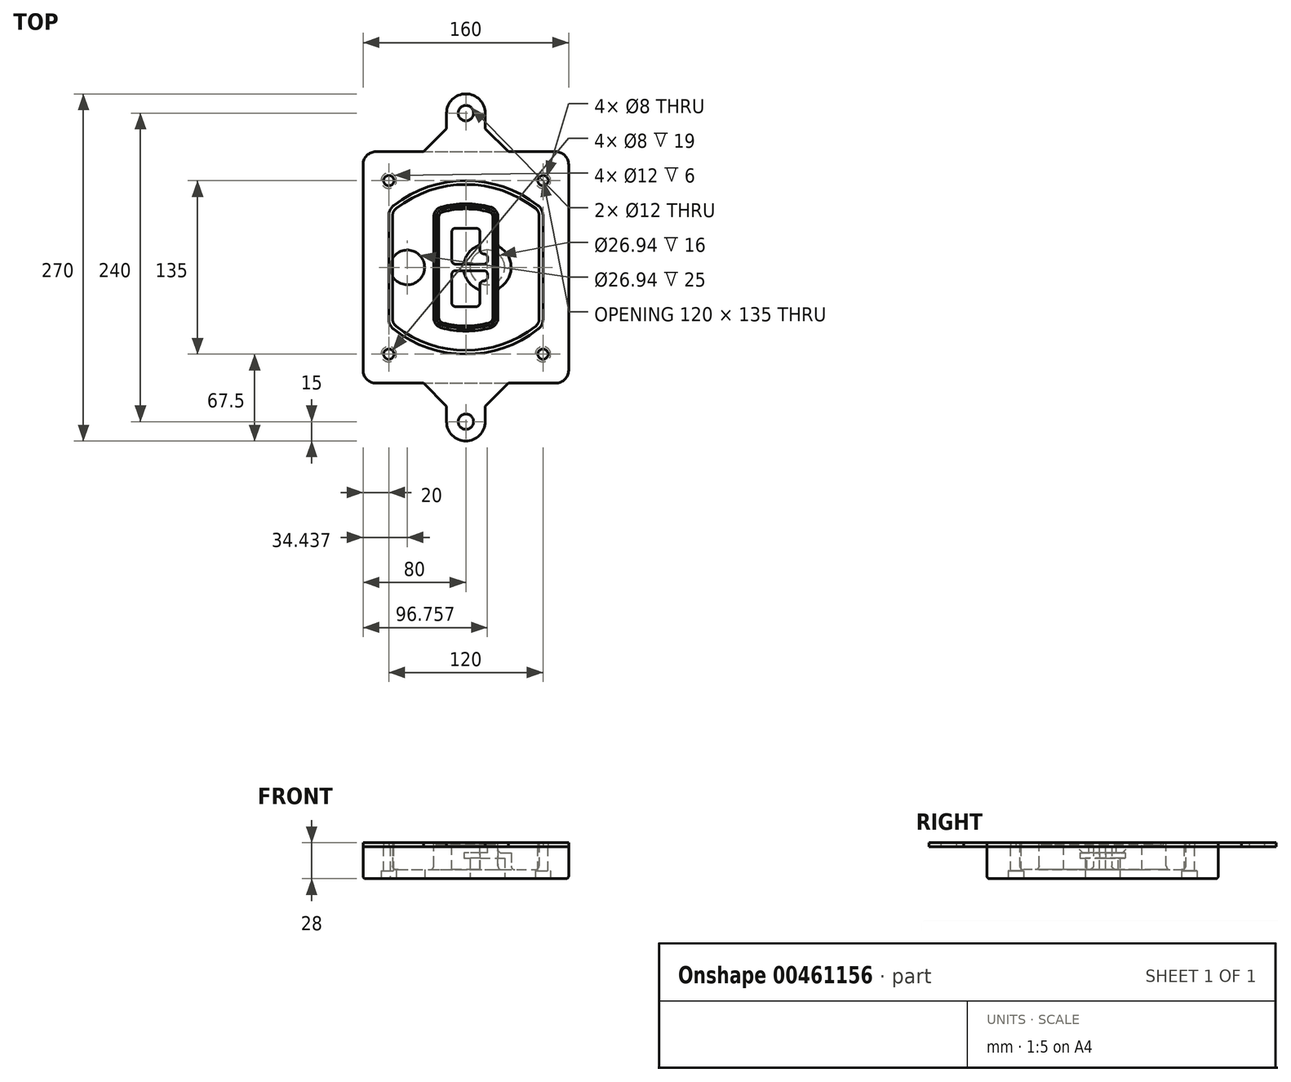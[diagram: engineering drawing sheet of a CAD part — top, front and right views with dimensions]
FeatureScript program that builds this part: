
annotation { "Feature Type Name" : "Feature", "Feature Type Description" : "" }
export const myFeature = defineFeature(function(context is Context, id is Id, definition is map)
    precondition{}
    {
        {
            var Q0;
            Q0=qCreatedBy(makeId("Top.planeOp"),FACE);
            var sketch = newSketch(context, id + "F0", { "sketchPlane" : qUnion([Q0])});
            skPoint(sketch, "E0.rect.middle", {"position": v(0, 0) * mm});
            skLineSegment(sketch, "E1.bottom", {"start": v(-70, -90) * mm, "end": v(70, -90) * mm});
            skLineSegment(sketch, "E1.top", {"start": v(-70, 90) * mm, "end": v(70, 90) * mm});
            skLineSegment(sketch, "E1.left", {"start": v(-80, -80) * mm, "end": v(-80, 80) * mm});
            skLineSegment(sketch, "E1.right", {"start": v(80, -80) * mm, "end": v(80, 80) * mm});
            skLineSegment(sketch, "E2", {"start": v(-80, 90) * mm, "end": v(80, -90) * mm, "construction": true});
            skLineSegment(sketch, "E3", {"start": v(80, 90) * mm, "end": v(-80, -90) * mm, "construction": true});
            skCircle(sketch, "E4", {"center": v(-60, 67.5) * mm, "radius": 4 * mm});
            skCircle(sketch, "E5", {"center": v(60, 67.5) * mm, "radius": 4 * mm});
            skCircle(sketch, "E6", {"center": v(60, -67.5) * mm, "radius": 4 * mm});
            skCircle(sketch, "E7", {"center": v(-60, -67.5) * mm, "radius": 4 * mm});
            skLineSegment(sketch, "E8", {"start": v(-60, 67.5) * mm, "end": v(60, 67.5) * mm, "construction": true});
            skLineSegment(sketch, "E9", {"start": v(60, 67.5) * mm, "end": v(60, -67.5) * mm, "construction": true});
            skLineSegment(sketch, "E10", {"start": v(60, -67.5) * mm, "end": v(-60, -67.5) * mm, "construction": true});
            skLineSegment(sketch, "E11", {"start": v(-60, -67.5) * mm, "end": v(-60, 67.5) * mm, "construction": true});
            skLineSegment(sketch, "E12", {"start": v(-60, 40.3) * mm, "end": v(-60, -40.3) * mm});
            skLineSegment(sketch, "E13", {"start": v(60, 40.3) * mm, "end": v(60, -40.3) * mm});
            skArc(sketch, "E14", {"start": v(56.15, 48.18) * mm, "mid": v(0, 67.5) * mm, "end": v(-56.15, 48.18) * mm});
            skArc(sketch, "E15", {"start": v(-56.15, -48.18) * mm, "mid": v(0, -67.5) * mm, "end": v(56.15, -48.18) * mm});
            skLineSegment(sketch, "E16", {"start": v(-60, 0) * mm, "end": v(60, 0) * mm, "construction": true});
            skPoint(sketch, "E17.visualSharp", {"position": v(-60, -45) * mm});
            skArc(sketch, "E17.filletArc", {"start": v(-60, -40.3) * mm, "mid": v(-58.99, -44.68) * mm, "end": v(-56.15, -48.18) * mm});
            skPoint(sketch, "E18.visualSharp", {"position": v(-60, 45) * mm});
            skArc(sketch, "E18.filletArc", {"start": v(-56.15, 48.18) * mm, "mid": v(-58.99, 44.68) * mm, "end": v(-60, 40.3) * mm});
            skPoint(sketch, "E19.visualSharp", {"position": v(60, 45) * mm});
            skArc(sketch, "E19.filletArc", {"start": v(60, 40.3) * mm, "mid": v(58.99, 44.68) * mm, "end": v(56.15, 48.18) * mm});
            skPoint(sketch, "E20.visualSharp", {"position": v(60, -45) * mm});
            skArc(sketch, "E20.filletArc", {"start": v(56.15, -48.18) * mm, "mid": v(58.99, -44.68) * mm, "end": v(60, -40.3) * mm});
            skPoint(sketch, "E21.visualSharp", {"position": v(-80, 90) * mm});
            skArc(sketch, "E21.filletArc", {"start": v(-70, 90) * mm, "mid": v(-77.07, 87.07) * mm, "end": v(-80, 80) * mm});
            skPoint(sketch, "E22.visualSharp", {"position": v(80, 90) * mm});
            skArc(sketch, "E22.filletArc", {"start": v(80, 80) * mm, "mid": v(77.07, 87.07) * mm, "end": v(70, 90) * mm});
            skPoint(sketch, "E23.visualSharp", {"position": v(80, -90) * mm});
            skArc(sketch, "E23.filletArc", {"start": v(70, -90) * mm, "mid": v(77.07, -87.07) * mm, "end": v(80, -80) * mm});
            skPoint(sketch, "E24.visualSharp", {"position": v(-80, -90) * mm});
            skArc(sketch, "E24.filletArc", {"start": v(-80, -80) * mm, "mid": v(-77.07, -87.07) * mm, "end": v(-70, -90) * mm});
            skArc(sketch, "E25.0", {"start": v(57, 40.3) * mm, "mid": v(56.3, 43.36) * mm, "end": v(54.3, 45.81) * mm});
            skLineSegment(sketch, "E25.1", {"start": v(57, 40.3) * mm, "end": v(57, -40.3) * mm});
            skArc(sketch, "E25.2", {"start": v(54.3, -45.81) * mm, "mid": v(56.3, -43.36) * mm, "end": v(57, -40.3) * mm});
            skArc(sketch, "E25.3", {"start": v(-54.3, -45.81) * mm, "mid": v(0, -64.5) * mm, "end": v(54.3, -45.81) * mm});
            skArc(sketch, "E25.4", {"start": v(-57, -40.3) * mm, "mid": v(-56.3, -43.36) * mm, "end": v(-54.3, -45.81) * mm});
            skArc(sketch, "E25.5", {"start": v(54.3, 45.81) * mm, "mid": v(0, 64.5) * mm, "end": v(-54.3, 45.81) * mm});
            skLineSegment(sketch, "E25.6", {"start": v(-57, 40.3) * mm, "end": v(-57, -40.3) * mm});
            skArc(sketch, "E25.7", {"start": v(-54.3, 45.81) * mm, "mid": v(-56.3, 43.36) * mm, "end": v(-57, 40.3) * mm});
            skArc(sketch, "E26.0", {"start": v(-58.62, 51.33) * mm, "mid": v(-62.58, 46.43) * mm, "end": v(-64, 40.3) * mm});
            skArc(sketch, "E26.1", {"start": v(58.62, 51.33) * mm, "mid": v(0, 71.5) * mm, "end": v(-58.62, 51.33) * mm});
            skArc(sketch, "E26.2", {"start": v(64, 40.3) * mm, "mid": v(62.58, 46.43) * mm, "end": v(58.62, 51.33) * mm});
            skLineSegment(sketch, "E26.3", {"start": v(64, 40.3) * mm, "end": v(64, -40.3) * mm});
            skArc(sketch, "E26.4", {"start": v(58.62, -51.33) * mm, "mid": v(62.58, -46.43) * mm, "end": v(64, -40.3) * mm});
            skLineSegment(sketch, "E26.5", {"start": v(-64, 40.3) * mm, "end": v(-64, -40.3) * mm});
            skArc(sketch, "E26.6", {"start": v(-58.62, -51.33) * mm, "mid": v(0, -71.5) * mm, "end": v(58.62, -51.33) * mm});
            skArc(sketch, "E26.7", {"start": v(-64, -40.3) * mm, "mid": v(-62.58, -46.43) * mm, "end": v(-58.62, -51.33) * mm});
            skSolve(sketch);
        }
        {
            var Q0;
            Q0=makeQuery(id+"F0.imprint","IMPRINT",FACE,{"disambiguationData":[TD([[makeQuery(id+"F0.imprint","IMPRINT",EDGE,{"derivedFrom":sQuery(id+"F0.wireOp",EDGE,"E1.bottom")}),1.0]])]});
            var Q1;
            Q1=makeQuery(id+"F0.imprint","IMPRINT",FACE,{"disambiguationData":[TD([[makeQuery(id+"F0.imprint","IMPRINT",EDGE,{"derivedFrom":sQuery(id+"F0.wireOp",EDGE,"E12")}),1.0]])]});
            var Q2;
            Q2=makeQuery(id+"F0.imprint","IMPRINT",FACE,{"disambiguationData":[TD([[makeQuery(id+"F0.imprint","IMPRINT",EDGE,{"derivedFrom":sQuery(id+"F0.wireOp",EDGE,"E25.0")}),1.0]])]});
            var Q3;
            Q3=makeQuery(id+"F0.imprint","IMPRINT",FACE,{"disambiguationData":[TD([[makeQuery(id+"F0.imprint","IMPRINT",EDGE,{"derivedFrom":sQuery(id+"F0.wireOp",EDGE,"E12")}),-1.0]])]});
            extrude(context, id + "F1", {"entities" : qUnion([Q0, Q1, Q2, Q3]), "oppositeDirection" : true, "depth" : 25 * mm});
        }
        {
            var Q0;
            Q0=makeQuery(id+"F0.imprint","IMPRINT",FACE,{"disambiguationData":[TD([[makeQuery(id+"F0.imprint","IMPRINT",EDGE,{"derivedFrom":sQuery(id+"F0.wireOp",EDGE,"E12")}),1.0]])]});
            extrude(context, id + "F2", {"entities" : qUnion([Q0]), "operationType" : NewBodyOperationType.ADD, "depth" : 3 * mm});
        }
        {
            var Q0;
            Q0=makeQuery(id+"F0.imprint","IMPRINT",FACE,{"disambiguationData":[TD([[makeQuery(id+"F0.imprint","IMPRINT",EDGE,{"derivedFrom":sQuery(id+"F0.wireOp",EDGE,"E25.0")}),1.0]])]});
            extrude(context, id + "F3", {"entities" : qUnion([Q0]), "operationType" : NewBodyOperationType.REMOVE, "oppositeDirection" : true, "depth" : 18 * mm});
        }
        {
            var Q0;
            Q0=makeQuery(id+"F2.opExtrude","CAP_FACE",FACE,{"disambiguationData":[OSD([sQuery(id+"F0.wireOp",EDGE,"E12"),sQuery(id+"F0.wireOp",EDGE,"E13"),sQuery(id+"F0.wireOp",EDGE,"E14"),sQuery(id+"F0.wireOp",EDGE,"E15"),sQuery(id+"F0.wireOp",EDGE,"E17.filletArc"),sQuery(id+"F0.wireOp",EDGE,"E18.filletArc"),sQuery(id+"F0.wireOp",EDGE,"E19.filletArc"),sQuery(id+"F0.wireOp",EDGE,"E20.filletArc"),sQuery(id+"F0.wireOp",EDGE,"E25.0"),sQuery(id+"F0.wireOp",EDGE,"E25.1"),sQuery(id+"F0.wireOp",EDGE,"E25.2"),sQuery(id+"F0.wireOp",EDGE,"E25.3"),sQuery(id+"F0.wireOp",EDGE,"E25.4"),sQuery(id+"F0.wireOp",EDGE,"E25.5"),sQuery(id+"F0.wireOp",EDGE,"E25.6"),sQuery(id+"F0.wireOp",EDGE,"E25.7")])],"isStart":false});
            var sketch = newSketch(context, id + "F4", { "sketchPlane" : qUnion([Q0])});
            skArc(sketch, "E27.0", {"start": v(-19.08, -46.97) * mm, "mid": v(0, -49.5) * mm, "end": v(19.08, -46.97) * mm});
            skArc(sketch, "E28.0", {"start": v(19.08, 46.97) * mm, "mid": v(0, 49.5) * mm, "end": v(-19.08, 46.97) * mm});
            skLineSegment(sketch, "E29", {"start": v(-25, 39.25) * mm, "end": v(-25, -39.25) * mm});
            skLineSegment(sketch, "E30", {"start": v(25, 39.25) * mm, "end": v(25, -39.25) * mm});
            skLineSegment(sketch, "E31", {"start": v(-25, 45.1) * mm, "end": v(25, 45.1) * mm, "construction": true});
            skLineSegment(sketch, "E32", {"start": v(-25, -45.1) * mm, "end": v(25, -45.1) * mm, "construction": true});
            skPoint(sketch, "E33.visualSharp", {"position": v(-25, 45.1) * mm});
            skArc(sketch, "E33.filletArc", {"start": v(-19.08, 46.97) * mm, "mid": v(-23.35, 44.11) * mm, "end": v(-25, 39.25) * mm});
            skPoint(sketch, "E34.visualSharp", {"position": v(25, 45.1) * mm});
            skArc(sketch, "E34.filletArc", {"start": v(25, 39.25) * mm, "mid": v(23.35, 44.11) * mm, "end": v(19.08, 46.97) * mm});
            skPoint(sketch, "E35.visualSharp", {"position": v(25, -45.1) * mm});
            skArc(sketch, "E35.filletArc", {"start": v(19.08, -46.97) * mm, "mid": v(23.35, -44.11) * mm, "end": v(25, -39.25) * mm});
            skPoint(sketch, "E36.visualSharp", {"position": v(-25, -45.1) * mm});
            skArc(sketch, "E36.filletArc", {"start": v(-25, -39.25) * mm, "mid": v(-23.35, -44.11) * mm, "end": v(-19.08, -46.97) * mm});
            skArc(sketch, "E37.0", {"start": v(54.3, 45.81) * mm, "mid": v(0, 64.5) * mm, "end": v(-54.3, 45.81) * mm});
            skArc(sketch, "E37.1", {"start": v(-54.3, 45.81) * mm, "mid": v(-56.3, 43.36) * mm, "end": v(-57, 40.3) * mm});
            skLineSegment(sketch, "E37.2", {"start": v(-57, 40.3) * mm, "end": v(-57, -40.3) * mm});
            skArc(sketch, "E37.3", {"start": v(-57, -40.3) * mm, "mid": v(-56.3, -43.36) * mm, "end": v(-54.3, -45.81) * mm});
            skArc(sketch, "E37.4", {"start": v(-54.3, -45.81) * mm, "mid": v(0, -64.5) * mm, "end": v(54.3, -45.81) * mm});
            skArc(sketch, "E37.5", {"start": v(54.3, -45.81) * mm, "mid": v(56.3, -43.36) * mm, "end": v(57, -40.3) * mm});
            skLineSegment(sketch, "E37.6", {"start": v(57, 40.3) * mm, "end": v(57, -40.3) * mm});
            skArc(sketch, "E37.7", {"start": v(57, 40.3) * mm, "mid": v(56.3, 43.36) * mm, "end": v(54.3, 45.81) * mm});
            skLineSegment(sketch, "E38.0", {"start": v(23, 39.25) * mm, "end": v(23, -39.25) * mm});
            skArc(sketch, "E38.1", {"start": v(18.56, -45.04) * mm, "mid": v(21.76, -42.9) * mm, "end": v(23, -39.25) * mm});
            skArc(sketch, "E38.2", {"start": v(-18.56, -45.04) * mm, "mid": v(0, -47.5) * mm, "end": v(18.56, -45.04) * mm});
            skArc(sketch, "E38.3", {"start": v(-23, -39.25) * mm, "mid": v(-21.76, -42.9) * mm, "end": v(-18.56, -45.04) * mm});
            skLineSegment(sketch, "E38.4", {"start": v(-23, 39.25) * mm, "end": v(-23, -39.25) * mm});
            skArc(sketch, "E38.5", {"start": v(23, 39.25) * mm, "mid": v(21.76, 42.9) * mm, "end": v(18.56, 45.04) * mm});
            skArc(sketch, "E38.6", {"start": v(-18.56, 45.04) * mm, "mid": v(-21.76, 42.9) * mm, "end": v(-23, 39.25) * mm});
            skArc(sketch, "E38.7", {"start": v(18.56, 45.04) * mm, "mid": v(0, 47.5) * mm, "end": v(-18.56, 45.04) * mm});
            skArc(sketch, "E39.0", {"start": v(21, 39.25) * mm, "mid": v(20.18, 41.68) * mm, "end": v(18.04, 43.1) * mm});
            skLineSegment(sketch, "E39.1", {"start": v(21, 39.25) * mm, "end": v(21, -39.25) * mm});
            skArc(sketch, "E39.2", {"start": v(18.04, -43.1) * mm, "mid": v(20.18, -41.68) * mm, "end": v(21, -39.25) * mm});
            skArc(sketch, "E39.3", {"start": v(-18.04, -43.1) * mm, "mid": v(0, -45.5) * mm, "end": v(18.04, -43.1) * mm});
            skArc(sketch, "E39.4", {"start": v(-21, -39.25) * mm, "mid": v(-20.18, -41.68) * mm, "end": v(-18.04, -43.1) * mm});
            skArc(sketch, "E39.5", {"start": v(18.04, 43.1) * mm, "mid": v(0, 45.5) * mm, "end": v(-18.04, 43.1) * mm});
            skLineSegment(sketch, "E39.6", {"start": v(-21, 39.25) * mm, "end": v(-21, -39.25) * mm});
            skArc(sketch, "E39.7", {"start": v(-18.04, 43.1) * mm, "mid": v(-20.18, 41.68) * mm, "end": v(-21, 39.25) * mm});
            skLineSegment(sketch, "E40", {"start": v(-25, 0) * mm, "end": v(25, 0) * mm, "construction": true});
            skLineSegment(sketch, "E41", {"start": v(-11, 5.5) * mm, "end": v(-11, 27.5) * mm});
            skLineSegment(sketch, "E42", {"start": v(-8, 30.5) * mm, "end": v(8, 30.5) * mm});
            skLineSegment(sketch, "E43", {"start": v(11, 27.5) * mm, "end": v(11, 13.5) * mm});
            skLineSegment(sketch, "E44", {"start": v(14, 10.5) * mm, "end": v(14, 10.5) * mm});
            skLineSegment(sketch, "E45", {"start": v(17, 7.5) * mm, "end": v(17, 5.5) * mm});
            skLineSegment(sketch, "E46", {"start": v(14, 2.5) * mm, "end": v(-8, 2.5) * mm});
            skPoint(sketch, "E47.visualSharp", {"position": v(-11, 30.5) * mm});
            skArc(sketch, "E47.filletArc", {"start": v(-8, 30.5) * mm, "mid": v(-10.12, 29.62) * mm, "end": v(-11, 27.5) * mm});
            skPoint(sketch, "E48.visualSharp", {"position": v(11, 30.5) * mm});
            skArc(sketch, "E48.filletArc", {"start": v(11, 27.5) * mm, "mid": v(10.12, 29.62) * mm, "end": v(8, 30.5) * mm});
            skPoint(sketch, "E49.visualSharp", {"position": v(11, 10.5) * mm});
            skArc(sketch, "E49.filletArc", {"start": v(11, 13.5) * mm, "mid": v(11.88, 11.38) * mm, "end": v(14, 10.5) * mm});
            skPoint(sketch, "E50.visualSharp", {"position": v(17, 10.5) * mm});
            skArc(sketch, "E50.filletArc", {"start": v(17, 7.5) * mm, "mid": v(16.12, 9.62) * mm, "end": v(14, 10.5) * mm});
            skPoint(sketch, "E51.visualSharp", {"position": v(17, 2.5) * mm});
            skArc(sketch, "E51.filletArc", {"start": v(14, 2.5) * mm, "mid": v(16.12, 3.38) * mm, "end": v(17, 5.5) * mm});
            skPoint(sketch, "E52.visualSharp", {"position": v(-11, 2.5) * mm});
            skArc(sketch, "E52.filletArc", {"start": v(-11, 5.5) * mm, "mid": v(-10.12, 3.38) * mm, "end": v(-8, 2.5) * mm});
            skLineSegment(sketch, "E53.0.MirrorCS", {"start": v(14, -2.5) * mm, "end": v(-8, -2.5) * mm});
            skArc(sketch, "E54.0.MirrorCS", {"start": v(-11, -5.5) * mm, "mid": v(-10.12, -3.38) * mm, "end": v(-8, -2.5) * mm});
            skLineSegment(sketch, "E55.0.MirrorCS", {"start": v(-11, -5.5) * mm, "end": v(-11, -27.5) * mm});
            skArc(sketch, "E56.0.MirrorCS", {"start": v(-8, -30.5) * mm, "mid": v(-10.12, -29.62) * mm, "end": v(-11, -27.5) * mm});
            skLineSegment(sketch, "E57.0.MirrorCS", {"start": v(-8, -30.5) * mm, "end": v(8, -30.5) * mm});
            skArc(sketch, "E58.0.MirrorCS", {"start": v(11, -27.5) * mm, "mid": v(10.12, -29.62) * mm, "end": v(8, -30.5) * mm});
            skLineSegment(sketch, "E59.0.MirrorCS", {"start": v(11, -27.5) * mm, "end": v(11, -13.5) * mm});
            skArc(sketch, "E60.0.MirrorCS", {"start": v(11, -13.5) * mm, "mid": v(11.88, -11.38) * mm, "end": v(14, -10.5) * mm});
            skArc(sketch, "E61.0.MirrorCS", {"start": v(17, -7.5) * mm, "mid": v(16.12, -9.62) * mm, "end": v(14, -10.5) * mm});
            skLineSegment(sketch, "E62.0.MirrorCS", {"start": v(17, -7.5) * mm, "end": v(17, -5.5) * mm});
            skArc(sketch, "E63.0.MirrorCS", {"start": v(14, -2.5) * mm, "mid": v(16.12, -3.38) * mm, "end": v(17, -5.5) * mm});
            skSolve(sketch);
        }
        {
            var Q0;
            Q0=makeQuery(id+"F4.imprint","IMPRINT",FACE,{"disambiguationData":[TD([[makeQuery(id+"F4.imprint","IMPRINT",EDGE,{"derivedFrom":sQuery(id+"F4.wireOp",EDGE,"E27.0")}),1.0]])]});
            var Q1;
            Q1=makeQuery(id+"F4.imprint","IMPRINT",FACE,{"disambiguationData":[TD([[makeQuery(id+"F4.imprint","IMPRINT",EDGE,{"derivedFrom":sQuery(id+"F4.wireOp",EDGE,"E38.0")}),-1.0]])]});
            var Q2;
            Q2=makeQuery(id+"F4.imprint","IMPRINT",FACE,{"disambiguationData":[TD([[makeQuery(id+"F4.imprint","IMPRINT",EDGE,{"derivedFrom":sQuery(id+"F4.wireOp",EDGE,"E39.0")}),1.0]])]});
            extrude(context, id + "F5", {"entities" : qUnion([Q0, Q1, Q2]), "operationType" : NewBodyOperationType.ADD, "endBound" : BoundingType.UP_TO_NEXT, "oppositeDirection" : true, "depth" : 25 * mm});
        }
        {
            var Q0;
            Q0=makeQuery(id+"F4.imprint","IMPRINT",FACE,{"disambiguationData":[TD([[makeQuery(id+"F4.imprint","IMPRINT",EDGE,{"derivedFrom":sQuery(id+"F4.wireOp",EDGE,"E38.0")}),-1.0]])]});
            extrude(context, id + "F6", {"entities" : qUnion([Q0]), "operationType" : NewBodyOperationType.REMOVE, "oppositeDirection" : true, "depth" : 2 * mm});
        }
        {
            var Q0;
            Q0=makeQuery(id+"F1.opExtrude","CAP_FACE",FACE,{"disambiguationData":[OSD([sQuery(id+"F0.wireOp",EDGE,"E1.bottom"),sQuery(id+"F0.wireOp",EDGE,"E1.top"),sQuery(id+"F0.wireOp",EDGE,"E1.left"),sQuery(id+"F0.wireOp",EDGE,"E1.right"),sQuery(id+"F0.wireOp",EDGE,"E4"),sQuery(id+"F0.wireOp",EDGE,"E5"),sQuery(id+"F0.wireOp",EDGE,"E6"),sQuery(id+"F0.wireOp",EDGE,"E7"),sQuery(id+"F0.wireOp",EDGE,"E21.filletArc"),sQuery(id+"F0.wireOp",EDGE,"E22.filletArc"),sQuery(id+"F0.wireOp",EDGE,"E23.filletArc"),sQuery(id+"F0.wireOp",EDGE,"E24.filletArc")])],"isStart":false});
            var sketch = newSketch(context, id + "F7", { "sketchPlane" : qUnion([Q0])});
            skCircle(sketch, "E64", {"center": v(16.76, 0) * mm, "radius": 13.47 * mm});
            skCircle(sketch, "E65", {"center": v(-45.56, 0) * mm, "radius": 13.47 * mm});
            skLineSegment(sketch, "E66", {"start": v(80, 0) * mm, "end": v(-80, 0) * mm});
            skCircle(sketch, "E67", {"center": v(16.76, 0) * mm, "radius": 18.47 * mm});
            skCircle(sketch, "E68", {"center": v(60, -67.5) * mm, "radius": 6 * mm});
            skCircle(sketch, "E69", {"center": v(-60, -67.5) * mm, "radius": 6 * mm});
            skCircle(sketch, "E70", {"center": v(-60, 67.5) * mm, "radius": 6 * mm});
            skCircle(sketch, "E71", {"center": v(60, 67.5) * mm, "radius": 6 * mm});
            skSolve(sketch);
        }
        {
            var Q0;
            {var subQ1=sQuery(id+"F7.wireOp",EDGE,"E66");var subQ4=sQuery(id+"F7.wireOp",EDGE,"E64");var subQ6=makeQuery(id+"F7.imprint","INTERSECT",VERTEX,{"disambiguationData":[OD(0.0)],"derivedFrom":[subQ4,subQ1]});Q0=makeQuery(id+"F7.imprint","IMPRINT",FACE,{"disambiguationData":[TD([[makeQuery(id+"F7.imprint","IMPRINT",EDGE,{"disambiguationData":[TD([[subQ6,-1.0]])],"derivedFrom":subQ4}),-1.0]])]});}
            var Q1;
            {var subQ0=sQuery(id+"F7.wireOp",EDGE,"E66");var subQ1=sQuery(id+"F7.wireOp",EDGE,"E64");var subQ3=makeQuery(id+"F7.imprint","INTERSECT",VERTEX,{"disambiguationData":[OD(0.0)],"derivedFrom":[subQ1,subQ0]});Q1=makeQuery(id+"F7.imprint","IMPRINT",FACE,{"disambiguationData":[TD([[makeQuery(id+"F7.imprint","IMPRINT",EDGE,{"disambiguationData":[TD([[subQ3,-1.0]])],"derivedFrom":subQ1}),1.0]])]});}
            var Q2;
            {var subQ0=sQuery(id+"F7.wireOp",EDGE,"E66");var subQ1=sQuery(id+"F7.wireOp",EDGE,"E64");var subQ3=makeQuery(id+"F7.imprint","INTERSECT",VERTEX,{"disambiguationData":[OD(0.0)],"derivedFrom":[subQ1,subQ0]});Q2=makeQuery(id+"F7.imprint","IMPRINT",FACE,{"disambiguationData":[TD([[makeQuery(id+"F7.imprint","IMPRINT",EDGE,{"disambiguationData":[TD([[subQ3,1.0]])],"derivedFrom":subQ1}),1.0]])]});}
            var Q3;
            {var subQ1=sQuery(id+"F7.wireOp",EDGE,"E66");var subQ4=sQuery(id+"F7.wireOp",EDGE,"E64");var subQ6=makeQuery(id+"F7.imprint","INTERSECT",VERTEX,{"disambiguationData":[OD(0.0)],"derivedFrom":[subQ4,subQ1]});Q3=makeQuery(id+"F7.imprint","IMPRINT",FACE,{"disambiguationData":[TD([[makeQuery(id+"F7.imprint","IMPRINT",EDGE,{"disambiguationData":[TD([[subQ6,1.0]])],"derivedFrom":subQ4}),-1.0]])]});}
            extrude(context, id + "F8", {"entities" : qUnion([Q0, Q1, Q2, Q3]), "operationType" : NewBodyOperationType.ADD, "oppositeDirection" : true, "depth" : 20 * mm});
        }
        {
            var Q0;
            {var subQ0=sQuery(id+"F7.wireOp",EDGE,"E66");var subQ1=sQuery(id+"F7.wireOp",EDGE,"E64");var subQ3=makeQuery(id+"F7.imprint","INTERSECT",VERTEX,{"disambiguationData":[OD(0.0)],"derivedFrom":[subQ1,subQ0]});Q0=makeQuery(id+"F7.imprint","IMPRINT",FACE,{"disambiguationData":[TD([[makeQuery(id+"F7.imprint","IMPRINT",EDGE,{"disambiguationData":[TD([[subQ3,-1.0]])],"derivedFrom":subQ1}),1.0]])]});}
            var Q1;
            {var subQ0=sQuery(id+"F7.wireOp",EDGE,"E66");var subQ1=sQuery(id+"F7.wireOp",EDGE,"E64");var subQ3=makeQuery(id+"F7.imprint","INTERSECT",VERTEX,{"disambiguationData":[OD(0.0)],"derivedFrom":[subQ1,subQ0]});Q1=makeQuery(id+"F7.imprint","IMPRINT",FACE,{"disambiguationData":[TD([[makeQuery(id+"F7.imprint","IMPRINT",EDGE,{"disambiguationData":[TD([[subQ3,1.0]])],"derivedFrom":subQ1}),1.0]])]});}
            extrude(context, id + "F9", {"entities" : qUnion([Q0, Q1]), "operationType" : NewBodyOperationType.REMOVE, "oppositeDirection" : true, "depth" : 16 * mm});
        }
        {
            var Q0;
            {var subQ0=sQuery(id+"F7.wireOp",EDGE,"E66");var subQ1=sQuery(id+"F7.wireOp",EDGE,"E65");var subQ3=makeQuery(id+"F7.imprint","INTERSECT",VERTEX,{"disambiguationData":[OD(0.0)],"derivedFrom":[subQ1,subQ0]});Q0=makeQuery(id+"F7.imprint","IMPRINT",FACE,{"disambiguationData":[TD([[makeQuery(id+"F7.imprint","IMPRINT",EDGE,{"disambiguationData":[TD([[subQ3,-1.0]])],"derivedFrom":subQ1}),1.0]])]});}
            var Q1;
            {var subQ0=sQuery(id+"F7.wireOp",EDGE,"E66");var subQ1=sQuery(id+"F7.wireOp",EDGE,"E65");var subQ3=makeQuery(id+"F7.imprint","INTERSECT",VERTEX,{"disambiguationData":[OD(0.0)],"derivedFrom":[subQ1,subQ0]});Q1=makeQuery(id+"F7.imprint","IMPRINT",FACE,{"disambiguationData":[TD([[makeQuery(id+"F7.imprint","IMPRINT",EDGE,{"disambiguationData":[TD([[subQ3,1.0]])],"derivedFrom":subQ1}),1.0]])]});}
            extrude(context, id + "F10", {"entities" : qUnion([Q0, Q1]), "operationType" : NewBodyOperationType.REMOVE, "oppositeDirection" : true, "depth" : 25 * mm});
        }
        {
            var Q0;
            Q0=makeQuery(id+"F7.imprint","IMPRINT",FACE,{"disambiguationData":[TD([[makeQuery(id+"F7.imprint","IMPRINT",EDGE,{"derivedFrom":sQuery(id+"F7.wireOp",EDGE,"E68")}),1.0]])]});
            var Q1;
            Q1=makeQuery(id+"F7.imprint","IMPRINT",FACE,{"disambiguationData":[TD([[makeQuery(id+"F7.imprint","IMPRINT",EDGE,{"derivedFrom":makeQuery(id+"F1.opExtrude","CAP_EDGE",EDGE,{"disambiguationData":[OSD([sQuery(id+"F0.wireOp",EDGE,"E5")])],"isStart":false})}),-1.0]])]});
            var Q2;
            Q2=makeQuery(id+"F7.imprint","IMPRINT",FACE,{"disambiguationData":[TD([[makeQuery(id+"F7.imprint","IMPRINT",EDGE,{"derivedFrom":sQuery(id+"F7.wireOp",EDGE,"E69")}),1.0]])]});
            var Q3;
            Q3=makeQuery(id+"F7.imprint","IMPRINT",FACE,{"disambiguationData":[TD([[makeQuery(id+"F7.imprint","IMPRINT",EDGE,{"derivedFrom":makeQuery(id+"F1.opExtrude","CAP_EDGE",EDGE,{"disambiguationData":[OSD([sQuery(id+"F0.wireOp",EDGE,"E4")])],"isStart":false})}),-1.0]])]});
            var Q4;
            Q4=makeQuery(id+"F7.imprint","IMPRINT",FACE,{"disambiguationData":[TD([[makeQuery(id+"F7.imprint","IMPRINT",EDGE,{"derivedFrom":sQuery(id+"F7.wireOp",EDGE,"E70")}),1.0]])]});
            var Q5;
            Q5=makeQuery(id+"F7.imprint","IMPRINT",FACE,{"disambiguationData":[TD([[makeQuery(id+"F7.imprint","IMPRINT",EDGE,{"derivedFrom":makeQuery(id+"F1.opExtrude","CAP_EDGE",EDGE,{"disambiguationData":[OSD([sQuery(id+"F0.wireOp",EDGE,"E7")])],"isStart":false})}),-1.0]])]});
            var Q6;
            Q6=makeQuery(id+"F7.imprint","IMPRINT",FACE,{"disambiguationData":[TD([[makeQuery(id+"F7.imprint","IMPRINT",EDGE,{"derivedFrom":sQuery(id+"F7.wireOp",EDGE,"E71")}),1.0]])]});
            var Q7;
            Q7=makeQuery(id+"F7.imprint","IMPRINT",FACE,{"disambiguationData":[TD([[makeQuery(id+"F7.imprint","IMPRINT",EDGE,{"derivedFrom":makeQuery(id+"F1.opExtrude","CAP_EDGE",EDGE,{"disambiguationData":[OSD([sQuery(id+"F0.wireOp",EDGE,"E6")])],"isStart":false})}),-1.0]])]});
            extrude(context, id + "F11", {"entities" : qUnion([Q0, Q1, Q2, Q3, Q4, Q5, Q6, Q7]), "operationType" : NewBodyOperationType.REMOVE, "oppositeDirection" : true, "depth" : 6 * mm});
        }
        {
            var Q0;
            Q0=makeQuery(id+"F9.boolean.opBoolean","COPY",FACE,{"derivedFrom":makeQuery(id+"F9.opExtrude","CAP_FACE",FACE,{"disambiguationData":[OSD([sQuery(id+"F7.wireOp",EDGE,"E64")])],"isStart":false})});
            var sketch = newSketch(context, id + "F12", { "sketchPlane" : qUnion([Q0])});
            skArc(sketch, "E72.0", {"start": v(11, 17.55) * mm, "mid": v(2.57, 11.82) * mm, "end": v(-1.54, 2.5) * mm});
            skArc(sketch, "E72.1", {"start": v(-1.54, -2.5) * mm, "mid": v(2.57, -11.82) * mm, "end": v(11, -17.55) * mm});
            skLineSegment(sketch, "E73", {"start": v(-1.54, -2.5) * mm, "end": v(14, -2.5) * mm});
            skLineSegment(sketch, "E74.0", {"start": v(14, 2.5) * mm, "end": v(-1.54, 2.5) * mm});
            skArc(sketch, "E74.1", {"start": v(14, 2.5) * mm, "mid": v(16.12, 3.38) * mm, "end": v(17, 5.5) * mm});
            skLineSegment(sketch, "E74.2", {"start": v(17, 7.5) * mm, "end": v(17, 5.5) * mm});
            skArc(sketch, "E74.3", {"start": v(17, 7.5) * mm, "mid": v(16.12, 9.62) * mm, "end": v(14, 10.5) * mm});
            skArc(sketch, "E74.4", {"start": v(11, 13.5) * mm, "mid": v(11.88, 11.38) * mm, "end": v(14, 10.5) * mm});
            skLineSegment(sketch, "E74.5", {"start": v(11, 17.55) * mm, "end": v(11, 13.5) * mm});
            skLineSegment(sketch, "E74.7", {"start": v(14, -2.5) * mm, "end": v(-1.54, -2.5) * mm});
            skArc(sketch, "E74.8", {"start": v(14, -2.5) * mm, "mid": v(16.12, -3.38) * mm, "end": v(17, -5.5) * mm});
            skLineSegment(sketch, "E74.9", {"start": v(17, -7.5) * mm, "end": v(17, -5.5) * mm});
            skArc(sketch, "E74.10", {"start": v(17, -7.5) * mm, "mid": v(16.12, -9.62) * mm, "end": v(14, -10.5) * mm});
            skArc(sketch, "E74.11", {"start": v(11, -13.5) * mm, "mid": v(11.88, -11.38) * mm, "end": v(14, -10.5) * mm});
            skLineSegment(sketch, "E74.12", {"start": v(11, -17.55) * mm, "end": v(11, -13.5) * mm});
            skPoint(sketch, "E75.orphan", {"position": v(11, -27.5) * mm});
            skPoint(sketch, "E76.orphan", {"position": v(-8, -2.5) * mm});
            skPoint(sketch, "E77.orphan", {"position": v(-8, 2.5) * mm});
            skPoint(sketch, "E78.orphan", {"position": v(11, 27.5) * mm});
            skSolve(sketch);
        }
        {
            var Q0;
            {var subQ7=sQuery(id+"F12.wireOp",EDGE,"E72.0");var subQ14=sQuery(id+"F12.wireOp",EDGE,"E72.1");var subQ16=sQuery(id+"F12.wireOp",EDGE,"E74.1");var subQ18=sQuery(id+"F12.wireOp",EDGE,"E74.8");Q0=qUnion([makeQuery(id+"F12.imprint","IMPRINT",FACE,{"disambiguationData":[TD([[makeQuery(id+"F12.imprint","IMPRINT",EDGE,{"derivedFrom":subQ7}),1.0]])]}),makeQuery(id+"F12.imprint","IMPRINT",FACE,{"disambiguationData":[TD([[makeQuery(id+"F12.imprint","IMPRINT",EDGE,{"derivedFrom":subQ14}),1.0]])]}),makeQuery(id+"F12.imprint","IMPRINT",FACE,{"disambiguationData":[TD([[makeQuery(id+"F12.imprint","IMPRINT",EDGE,{"derivedFrom":subQ16}),1.0]])]}),makeQuery(id+"F12.imprint","IMPRINT",FACE,{"disambiguationData":[TD([[makeQuery(id+"F12.imprint","IMPRINT",EDGE,{"derivedFrom":subQ18}),-1.0]])]})]);}
            var Q1;
            Q1=makeQuery(id+"F5.boolean.opBoolean","SPLIT",FACE,{"disambiguationData":[TD([makeQuery(id+"F5.opExtrude","SWEPT_FACE",FACE,{"disambiguationData":[OSD([sQuery(id+"F4.wireOp",EDGE,"E41")])]})])],"derivedFrom":makeQuery(id+"F3.boolean.opBoolean","COPY",FACE,{"derivedFrom":makeQuery(id+"F3.opExtrude","CAP_FACE",FACE,{"disambiguationData":[OSD([sQuery(id+"F0.wireOp",EDGE,"E25.0"),sQuery(id+"F0.wireOp",EDGE,"E25.1"),sQuery(id+"F0.wireOp",EDGE,"E25.2"),sQuery(id+"F0.wireOp",EDGE,"E25.3"),sQuery(id+"F0.wireOp",EDGE,"E25.4"),sQuery(id+"F0.wireOp",EDGE,"E25.5"),sQuery(id+"F0.wireOp",EDGE,"E25.6"),sQuery(id+"F0.wireOp",EDGE,"E25.7")])],"isStart":false})})});
            extrude(context, id + "F13", {"entities" : qUnion([Q0]), "operationType" : NewBodyOperationType.REMOVE, "endBound" : BoundingType.UP_TO_SURFACE, "endBoundEntityFace" : qUnion([Q1]), "depth" : 25 * mm});
        }
        {
            var Q0;
            Q0=makeQuery(id+"F3.boolean.opBoolean","COPY",EDGE,{"derivedFrom":makeQuery(id+"F3.opExtrude","CAP_EDGE",EDGE,{"disambiguationData":[OSD([sQuery(id+"F0.wireOp",EDGE,"E25.6")])],"isStart":false})});
            var Q1;
            Q1=makeQuery(id+"F8.boolean.opBoolean","INTERSECT",EDGE,{"derivedFrom":[makeQuery(id+"F5.opExtrude","SWEPT_FACE",FACE,{"disambiguationData":[OSD([sQuery(id+"F4.wireOp",EDGE,"E30")])]}),makeQuery(id+"F8.opExtrude","CAP_FACE",FACE,{"disambiguationData":[OSD([sQuery(id+"F7.wireOp",EDGE,"E67")])],"isStart":false})]});
            var Q2;
            Q2=makeQuery(id+"F8.boolean.opBoolean","INTERSECT",EDGE,{"disambiguationData":[OD(1.0)],"derivedFrom":[makeQuery(id+"F5.opExtrude","SWEPT_FACE",FACE,{"disambiguationData":[OSD([sQuery(id+"F4.wireOp",EDGE,"E30")])]}),makeQuery(id+"F8.opExtrude","SWEPT_FACE",FACE,{"disambiguationData":[OSD([sQuery(id+"F7.wireOp",EDGE,"E67")])]})]});
            var Q3;
            {var subQ0=sQuery(id+"F4.wireOp",EDGE,"E30");Q3=makeQuery(id+"F8.boolean.opBoolean","SPLIT",EDGE,{"disambiguationData":[TD([makeQuery(id+"F5.opExtrude","SWEPT_FACE",FACE,{"disambiguationData":[OSD([sQuery(id+"F4.wireOp",EDGE,"E35.filletArc")])]})])],"derivedFrom":makeQuery(id+"F5.opExtrude","CAP_EDGE",EDGE,{"disambiguationData":[OSD([subQ0])],"isStart":false})});}
            var Q4;
            {var subQ0=sQuery(id+"F0.wireOp",EDGE,"E25.7");var subQ1=sQuery(id+"F0.wireOp",EDGE,"E25.1");var subQ2=sQuery(id+"F0.wireOp",EDGE,"E25.6");var subQ3=sQuery(id+"F0.wireOp",EDGE,"E25.5");var subQ4=sQuery(id+"F0.wireOp",EDGE,"E25.4");var subQ5=sQuery(id+"F0.wireOp",EDGE,"E25.0");var subQ6=sQuery(id+"F0.wireOp",EDGE,"E25.2");var subQ7=sQuery(id+"F0.wireOp",EDGE,"E25.3");Q4=makeQuery(id+"F8.boolean.opBoolean","INTERSECT",EDGE,{"derivedFrom":[makeQuery(id+"F5.boolean.opBoolean","SPLIT",FACE,{"disambiguationData":[TD([makeQuery(id+"F2.opExtrude","SWEPT_FACE",FACE,{"disambiguationData":[OSD([subQ5])]})])],"derivedFrom":makeQuery(id+"F3.boolean.opBoolean","COPY",FACE,{"derivedFrom":makeQuery(id+"F3.opExtrude","CAP_FACE",FACE,{"disambiguationData":[OSD([subQ5,subQ1,subQ6,subQ7,subQ4,subQ3,subQ2,subQ0])],"isStart":false})})}),makeQuery(id+"F8.opExtrude","SWEPT_FACE",FACE,{"disambiguationData":[OSD([sQuery(id+"F7.wireOp",EDGE,"E67")])]})]});}
            var Q5;
            Q5=makeQuery(id+"F8.boolean.opBoolean","INTERSECT",EDGE,{"disambiguationData":[OD(0.0)],"derivedFrom":[makeQuery(id+"F5.opExtrude","SWEPT_FACE",FACE,{"disambiguationData":[OSD([sQuery(id+"F4.wireOp",EDGE,"E30")])]}),makeQuery(id+"F8.opExtrude","SWEPT_FACE",FACE,{"disambiguationData":[OSD([sQuery(id+"F7.wireOp",EDGE,"E67")])]})]});
            fillet(context, id + "F14", {"entities" : qUnion([Q0, Q1, Q2, Q3, Q4, Q5]), "radius" : 3 * mm, "tangentPropagation" : true, "allowEdgeOverflow" : false});
        }
        {
            var Q0;
            Q0=makeQuery(id+"F1.opExtrude","CAP_EDGE",EDGE,{"disambiguationData":[OSD([sQuery(id+"F0.wireOp",EDGE,"E1.bottom")])],"isStart":false});
            fillet(context, id + "F15", {"entities" : qUnion([Q0]), "radius" : 2 * mm, "tangentPropagation" : true, "allowEdgeOverflow" : false});
        }
        {
            var Q0;
            {var subQ0=sQuery(id+"F0.wireOp",EDGE,"E21.filletArc");var subQ1=sQuery(id+"F0.wireOp",EDGE,"E7");var subQ2=sQuery(id+"F0.wireOp",EDGE,"E6");var subQ3=sQuery(id+"F0.wireOp",EDGE,"E5");var subQ4=sQuery(id+"F0.wireOp",EDGE,"E4");var subQ5=sQuery(id+"F0.wireOp",EDGE,"E22.filletArc");var subQ6=sQuery(id+"F0.wireOp",EDGE,"E1.bottom");var subQ7=sQuery(id+"F0.wireOp",EDGE,"E1.right");var subQ8=sQuery(id+"F0.wireOp",EDGE,"E1.top");var subQ9=sQuery(id+"F0.wireOp",EDGE,"E1.left");var subQ10=sQuery(id+"F0.wireOp",EDGE,"E23.filletArc");var subQ11=sQuery(id+"F0.wireOp",EDGE,"E24.filletArc");Q0=makeQuery(id+"F2.boolean.opBoolean","SPLIT",FACE,{"disambiguationData":[TD([makeQuery(id+"F1.opExtrude","SWEPT_FACE",FACE,{"disambiguationData":[OSD([subQ6])]})])],"derivedFrom":makeQuery(id+"F1.opExtrude","CAP_FACE",FACE,{"disambiguationData":[OSD([subQ6,subQ8,subQ9,subQ7,subQ4,subQ3,subQ2,subQ1,subQ0,subQ5,subQ10,subQ11])],"isStart":true})});}
            var sketch = newSketch(context, id + "F16", { "sketchPlane" : qUnion([Q0])});
            skLineSegment(sketch, "E79.0", {"start": v(-70, 90) * mm, "end": v(70, 90) * mm});
            skArc(sketch, "E79.1", {"start": v(80, 80) * mm, "mid": v(77.07, 87.07) * mm, "end": v(70, 90) * mm});
            skArc(sketch, "E79.2", {"start": v(-70, 90) * mm, "mid": v(-77.07, 87.07) * mm, "end": v(-80, 80) * mm});
            skLineSegment(sketch, "E79.3", {"start": v(-80, -80) * mm, "end": v(-80, 80) * mm});
            skLineSegment(sketch, "E79.4", {"start": v(80, -80) * mm, "end": v(80, 80) * mm});
            skArc(sketch, "E79.5", {"start": v(70, -90) * mm, "mid": v(77.07, -87.07) * mm, "end": v(80, -80) * mm});
            skLineSegment(sketch, "E79.6", {"start": v(-70, -90) * mm, "end": v(70, -90) * mm});
            skArc(sketch, "E79.7", {"start": v(-80, -80) * mm, "mid": v(-77.07, -87.07) * mm, "end": v(-70, -90) * mm});
            skCircle(sketch, "E79.8", {"center": v(-60, -67.5) * mm, "radius": 4 * mm});
            skCircle(sketch, "E79.9", {"center": v(-60, 67.5) * mm, "radius": 4 * mm});
            skCircle(sketch, "E79.10", {"center": v(60, 67.5) * mm, "radius": 4 * mm});
            skCircle(sketch, "E79.11", {"center": v(60, -67.5) * mm, "radius": 4 * mm});
            skArc(sketch, "E79.12", {"start": v(56.15, 48.18) * mm, "mid": v(0, 67.5) * mm, "end": v(-56.15, 48.18) * mm});
            skArc(sketch, "E79.13", {"start": v(60, 40.3) * mm, "mid": v(58.99, 44.68) * mm, "end": v(56.15, 48.18) * mm});
            skLineSegment(sketch, "E79.14", {"start": v(60, 40.3) * mm, "end": v(60, -40.3) * mm});
            skArc(sketch, "E79.15", {"start": v(-56.15, -48.18) * mm, "mid": v(0, -67.5) * mm, "end": v(56.15, -48.18) * mm});
            skArc(sketch, "E79.16", {"start": v(56.15, -48.18) * mm, "mid": v(58.99, -44.68) * mm, "end": v(60, -40.3) * mm});
            skArc(sketch, "E79.17", {"start": v(-60, -40.3) * mm, "mid": v(-58.99, -44.68) * mm, "end": v(-56.15, -48.18) * mm});
            skLineSegment(sketch, "E79.18", {"start": v(-60, 40.3) * mm, "end": v(-60, -40.3) * mm});
            skArc(sketch, "E79.19", {"start": v(-56.15, 48.18) * mm, "mid": v(-58.99, 44.68) * mm, "end": v(-60, 40.3) * mm});
            skPoint(sketch, "E79.20", {"position": v(77.07, -87.07) * mm});
            skCircle(sketch, "E80", {"center": v(0, 120) * mm, "radius": 6 * mm});
            skArc(sketch, "E81", {"start": v(15, 120) * mm, "mid": v(0, 135) * mm, "end": v(-15, 120) * mm});
            skLineSegment(sketch, "E82", {"start": v(-15, 108) * mm, "end": v(-33, 90) * mm});
            skLineSegment(sketch, "E83", {"start": v(-15, 120) * mm, "end": v(-15, 108) * mm});
            skLineSegment(sketch, "E84", {"start": v(15, 120) * mm, "end": v(15, 108) * mm});
            skLineSegment(sketch, "E85", {"start": v(15, 108) * mm, "end": v(33, 90) * mm});
            skLineSegment(sketch, "E86", {"start": v(-80, 0) * mm, "end": v(106.6, 0) * mm, "construction": true});
            skPoint(sketch, "E86.endSnap0", {"position": v(80, 0) * mm});
            skLineSegment(sketch, "E87.MirrorCS", {"start": v(15, -120) * mm, "end": v(15, -108) * mm});
            skLineSegment(sketch, "E88.MirrorCS", {"start": v(15, -108) * mm, "end": v(33, -90) * mm});
            skArc(sketch, "E89.MirrorCS", {"start": v(15, -120) * mm, "mid": v(0, -135) * mm, "end": v(-15, -120) * mm});
            skLineSegment(sketch, "E90.MirrorCS", {"start": v(-15, -120) * mm, "end": v(-15, -108) * mm});
            skLineSegment(sketch, "E91.MirrorCS", {"start": v(-15, -108) * mm, "end": v(-33, -90) * mm});
            skCircle(sketch, "E92.MirrorC", {"center": v(0, -120) * mm, "radius": 6 * mm});
            skLineSegment(sketch, "E93", {"start": v(0, 120) * mm, "end": v(0, 90) * mm, "construction": true});
            skSolve(sketch);
        }
        {
            var Q0;
            Q0 = qSketchRegion(id + "F16", true);
            var Q1;
            Q1=makeQuery(id+"F2.opExtrude","CAP_FACE",FACE,{"disambiguationData":[OSD([sQuery(id+"F0.wireOp",EDGE,"E12"),sQuery(id+"F0.wireOp",EDGE,"E13"),sQuery(id+"F0.wireOp",EDGE,"E14"),sQuery(id+"F0.wireOp",EDGE,"E15"),sQuery(id+"F0.wireOp",EDGE,"E17.filletArc"),sQuery(id+"F0.wireOp",EDGE,"E18.filletArc"),sQuery(id+"F0.wireOp",EDGE,"E19.filletArc"),sQuery(id+"F0.wireOp",EDGE,"E20.filletArc"),sQuery(id+"F0.wireOp",EDGE,"E25.0"),sQuery(id+"F0.wireOp",EDGE,"E25.1"),sQuery(id+"F0.wireOp",EDGE,"E25.2"),sQuery(id+"F0.wireOp",EDGE,"E25.3"),sQuery(id+"F0.wireOp",EDGE,"E25.4"),sQuery(id+"F0.wireOp",EDGE,"E25.5"),sQuery(id+"F0.wireOp",EDGE,"E25.6"),sQuery(id+"F0.wireOp",EDGE,"E25.7")])],"isStart":false});
            extrude(context, id + "F17", {"entities" : qUnion([Q0]), "endBound" : BoundingType.UP_TO_SURFACE, "endBoundEntityFace" : qUnion([Q1]), "depth" : 25 * mm});
        }
    });
